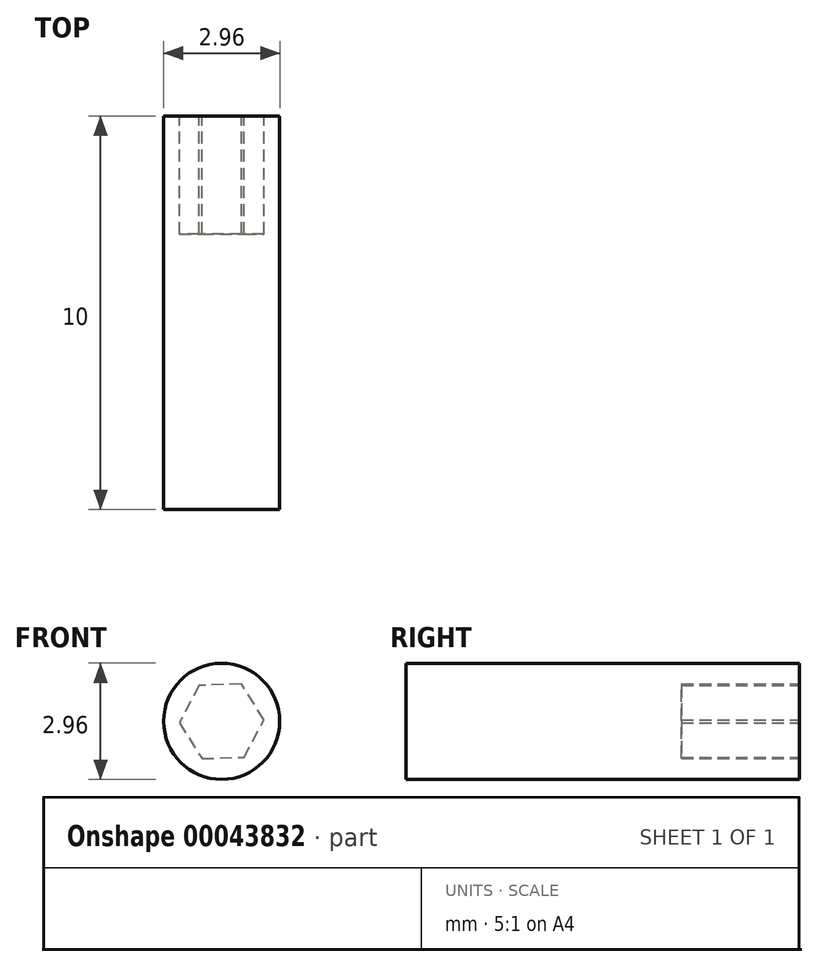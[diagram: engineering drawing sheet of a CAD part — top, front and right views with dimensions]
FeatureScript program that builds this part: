
annotation { "Feature Type Name" : "Feature", "Feature Type Description" : "" }
export const myFeature = defineFeature(function(context is Context, id is Id, definition is map)
    precondition{}
    {
        {
            var Q0;
            Q0=qCreatedBy(makeId("Front.planeOp"),FACE);
            var sketch = newSketch(context, id + "F0", { "sketchPlane" : qUnion([Q0])});
            skCircle(sketch, "E0", {"center": v(0, 0) * mm, "radius": 1.48 * mm});
            skSolve(sketch);
        }
        {
            var Q0;
            Q0 = qSketchRegion(id + "F0", true);
            extrude(context, id + "F1", {"entities" : qUnion([Q0]), "depth" : 10 * mm});
        }
        {
            var Q0;
            Q0=makeQuery(id+"F1.opExtrude","CAP_FACE",FACE,{"disambiguationData":[OSD([sQuery(id+"F0.wireOp",EDGE,"E0")])],"isStart":true});
            var sketch = newSketch(context, id + "F2", { "sketchPlane" : qUnion([Q0])});
            skCircle(sketch, "E1.cCircle", {"center": v(0, 0) * mm, "radius": 0.93 * mm, "construction": true});
            skLineSegment(sketch, "E1.0", {"start": v(-0.57, -0.91) * mm, "end": v(-1.07, 0.04) * mm});
            skLineSegment(sketch, "E1.1", {"start": v(-1.07, 0.04) * mm, "end": v(-0.5, 0.95) * mm});
            skLineSegment(sketch, "E1.2", {"start": v(-0.5, 0.95) * mm, "end": v(0.57, 0.91) * mm});
            skLineSegment(sketch, "E1.3", {"start": v(0.57, 0.91) * mm, "end": v(1.07, -0.04) * mm});
            skLineSegment(sketch, "E1.4", {"start": v(1.07, -0.04) * mm, "end": v(0.5, -0.95) * mm});
            skLineSegment(sketch, "E1.5", {"start": v(0.5, -0.95) * mm, "end": v(-0.57, -0.91) * mm});
            skPoint(sketch, "E1.0.midPoint", {"position": v(-0.82, -0.44) * mm});
            skSolve(sketch);
        }
        {
            var Q0;
            Q0 = qSketchRegion(id + "F2", true);
            extrude(context, id + "F3", {"entities" : qUnion([Q0]), "operationType" : NewBodyOperationType.REMOVE, "oppositeDirection" : true, "depth" : 3 * mm});
        }
    });
